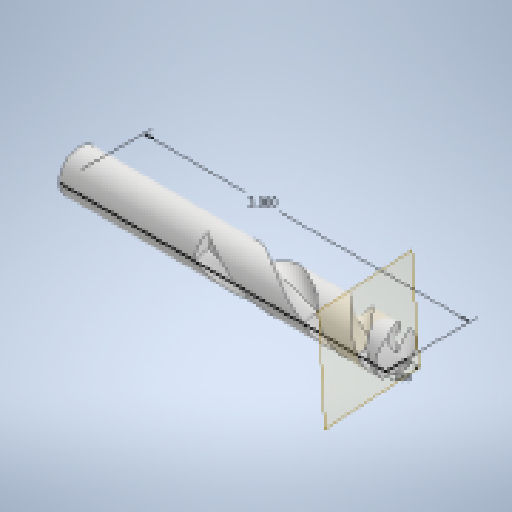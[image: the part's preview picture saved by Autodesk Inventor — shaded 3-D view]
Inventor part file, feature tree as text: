
AUTODESK INVENTOR PART (.ipt)
format: ipt  version: 2023 (Build 270158000, 158)  size: 265,216 bytes
history: native  units: in
note: dims shown in document units (in); Inventor stores cm internally (conversion verified against a paired STEP export)
features: sketch x5, helix x3, revolve x2, projected_geometry x2, plane x1, pattern_circular x1
ambient origin geometry x8: Origin, YZ Plane, XZ Plane, XY Plane, X Axis, Y Axis, Z Axis, Center Point
bodies: Solid1 (feature_tree)
feature tree (14):
  sketch  "Sketch1"  dims[d0=3.0in d1=0.1875in d2=90.0deg]
  revolve  "Revolution1"  [1 undecoded]
  helix  "Coil1"  [1 undecoded]
  plane  "Work Plane1"
  helix  "Coil2"  [1 undecoded]
  helix  "Coil3"  [1 undecoded]
  pattern_circular  "Circular Pattern2"  [2 undecoded]
  revolve  "Revolution3"  [1 undecoded]
  sketch  "Sketch4"  dims[d3=0.5in d4=1.0in d5=0.1969in d6=0.0in d7=90.0deg d8=90.0deg d9=0.0in d10=0.0in]
  sketch  "Sketch5"  dims[d14=1.0in d15=1.0in d16=0.1969in d17=0.0in d18=90.0deg d19=90.0deg d20=0.0in d21=0.0in]
  sketch  "Sketch6"  dims[d22=2.0in d23=1.0in d24=0.1969in d25=0.0in d26=90.0deg d27=90.0deg d28=0.0in d29=0.0in d30=0.7874in d31=360.0deg d33=1.0in]
  projected_geometry  "Projected Loop2"
  projected_geometry  "Projected Loop3"
  sketch  "Sketch8"  dims[d35=0.1454in d36=0.1749in d40=0.1875in d41=0.1718in d42=90.0deg]
note: 7 required parameter values undecoded (feature->parameter linkage not recoverable at this tier; creation-order binding heuristic only, values carry confidence <= 0.55)